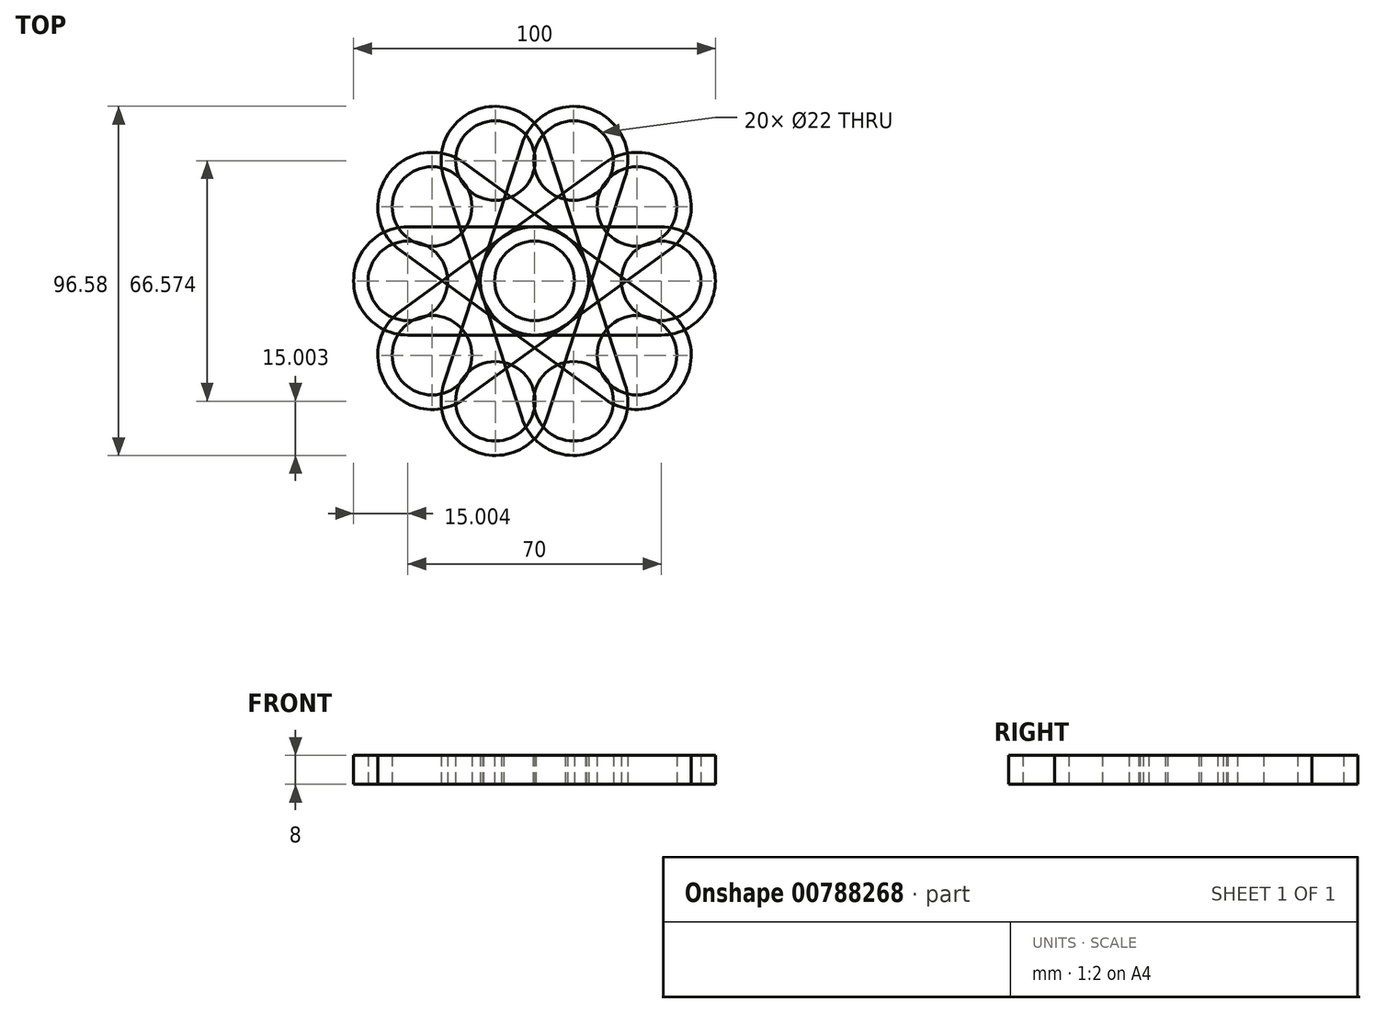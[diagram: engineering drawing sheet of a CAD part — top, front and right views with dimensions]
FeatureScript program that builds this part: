
annotation { "Feature Type Name" : "Feature", "Feature Type Description" : "" }
export const myFeature = defineFeature(function(context is Context, id is Id, definition is map)
    precondition{}
    {
        {
            var Q0;
            Q0=qCreatedBy(makeId("Top.planeOp"),FACE);
            var sketch = newSketch(context, id + "F0", { "sketchPlane" : qUnion([Q0])});
            skCircle(sketch, "E0", {"center": v(-20.5, 0) * mm, "radius": 11 * mm});
            skCircle(sketch, "E1", {"center": v(-20.5, 0) * mm, "radius": 15 * mm});
            skLineSegment(sketch, "E2", {"start": v(-20.5, 0) * mm, "end": v(14.5, 0) * mm, "construction": true});
            skCircle(sketch, "E3", {"center": v(14.5, 0) * mm, "radius": 11 * mm});
            skCircle(sketch, "E4", {"center": v(14.5, 0) * mm, "radius": 15 * mm});
            skLineSegment(sketch, "E5", {"start": v(-20.86, 15) * mm, "end": v(14.5, 15) * mm});
            skLineSegment(sketch, "E6", {"start": v(-20.5, 0) * mm, "end": v(-20.5, -15) * mm, "construction": true});
            skLineSegment(sketch, "E7", {"start": v(-20.5, -15) * mm, "end": v(14.5, -15) * mm});
            skSolve(sketch);
        }
        {
            var Q0;
            Q0=makeQuery(id+"F0.imprint","IMPRINT",FACE,{"disambiguationData":[TD([[makeQuery(id+"F0.imprint","IMPRINT",EDGE,{"derivedFrom":sQuery(id+"F0.wireOp",EDGE,"E0")}),-1.0]])]});
            var Q1;
            Q1=makeQuery(id+"F0.imprint","IMPRINT",FACE,{"disambiguationData":[TD([[makeQuery(id+"F0.imprint","IMPRINT",EDGE,{"derivedFrom":sQuery(id+"F0.wireOp",EDGE,"E3")}),-1.0]])]});
            var Q2;
            {var subQ0=sQuery(id+"F0.wireOp",EDGE,"E7");Q2=makeQuery(id+"F0.imprint","IMPRINT",FACE,{"disambiguationData":[TD([[makeQuery(id+"F0.imprint","IMPRINT",EDGE,{"derivedFrom":subQ0}),1.0]])]});}
            extrude(context, id + "F1", {"entities" : qUnion([Q0, Q1, Q2]), "depth" : 8 * mm, "offsetDistance" : 25 * mm});
        }
        {
            var Q0;
            Q0=makeQuery(id+"F1.opExtrude","SWEPT_BODY",BODY,{"disambiguationData":[OSD([sQuery(id+"F0.wireOp",EDGE,"E0"),sQuery(id+"F0.wireOp",EDGE,"E1"),sQuery(id+"F0.wireOp",EDGE,"E3"),sQuery(id+"F0.wireOp",EDGE,"E4"),sQuery(id+"F0.wireOp",EDGE,"E5"),sQuery(id+"F0.wireOp",EDGE,"E7")])]});
            var Q1;
            Q1=sQuery(id+"F0.wireOp",EDGE,"E0");
            circularPattern(context, id + "F2", {"entities" : qUnion([Q0]), "axis" : qUnion([Q1]), "angle" : 360 * degree, "instanceCount" : 10, "equalSpace" : true});
        }
    });
